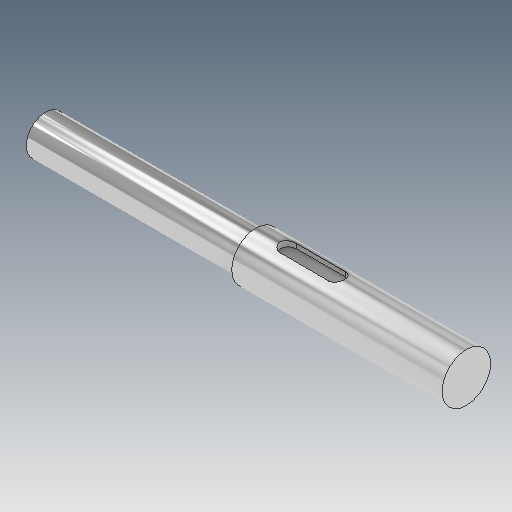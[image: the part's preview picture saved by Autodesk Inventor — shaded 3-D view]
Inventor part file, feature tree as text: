
AUTODESK INVENTOR PART (.ipt)
format: ipt  version: 2020.3 (Build 243373010, 373A)  size: 154,624 bytes
history: native  units: mm
features: other x5, revolve x1
ambient origin geometry x6: Origin, XZ Plane, XY Plane, X Axis, Y Axis, Z Axis
bodies: Solid1 (feature_tree)
feature tree (6):
  revolve  "Revolution1"  [1 undecoded]
  other  "Keyway1"
  other  "Start Plane"
  other  "Origin point"
  other  "Main Sketch"
  other  "iFeature3:1"
note: 1 required parameter value undecoded (feature->parameter linkage not recoverable at this tier; creation-order binding heuristic only, values carry confidence <= 0.55)
